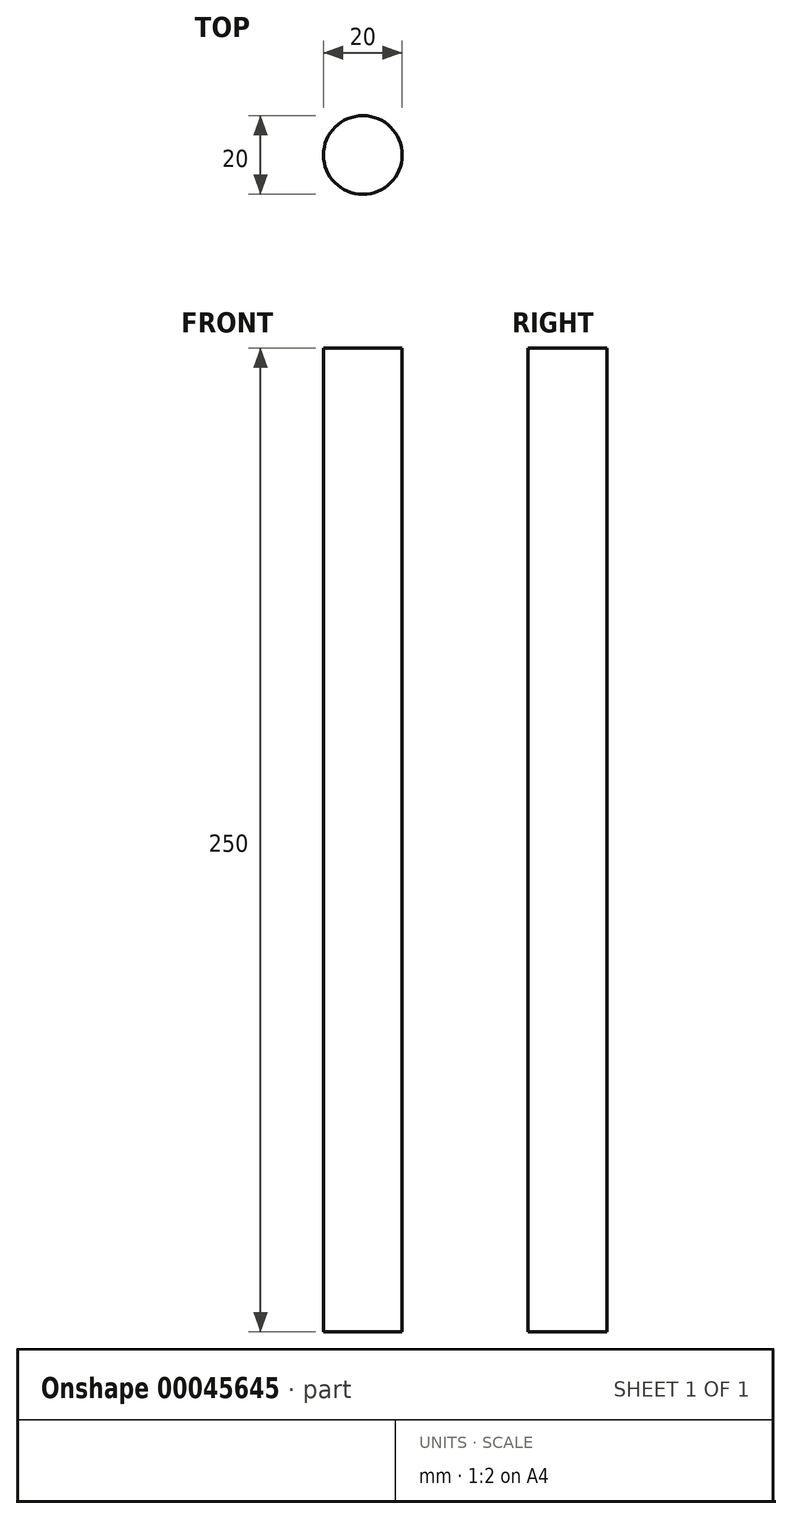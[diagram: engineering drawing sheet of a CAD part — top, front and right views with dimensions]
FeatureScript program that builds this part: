
annotation { "Feature Type Name" : "Feature", "Feature Type Description" : "" }
export const myFeature = defineFeature(function(context is Context, id is Id, definition is map)
    precondition{}
    {
        {
            var Q0;
            Q0=qCreatedBy(makeId("Top.planeOp"),FACE);
            var sketch = newSketch(context, id + "F0", { "sketchPlane" : qUnion([Q0])});
            skCircle(sketch, "E0", {"center": v(0, 0) * mm, "radius": 10 * mm});
            skSolve(sketch);
        }
        {
            var Q0;
            Q0=makeQuery(id+"F0.imprint","IMPRINT",FACE,{"disambiguationData":[TD([[makeQuery(id+"F0.imprint","IMPRINT",EDGE,{"derivedFrom":sQuery(id+"F0.wireOp",EDGE,"E0")}),1.0]])]});
            extrude(context, id + "F1", {"entities" : qUnion([Q0]), "depth" : 250 * mm});
        }
    });
